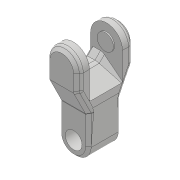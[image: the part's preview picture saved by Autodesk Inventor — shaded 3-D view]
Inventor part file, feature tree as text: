
AUTODESK INVENTOR PART (.ipt)
format: ipt  version: 2018 (Build 220112000, 112)  size: 823,296 bytes
history: native  units: mm
features: sketch x33, projected_geometry x33, extrude x31, chamfer x11, fillet x7, hole x3, mirror x1
ambient origin geometry x8: Origin, YZ Plane, XZ Plane, XY Plane, X Axis, Y Axis, Z Axis, Center Point
bodies: Solid1 (feature_tree)
feature tree (119):
  extrude  "Extrusion1"  Depth=45.0mm
  extrude  "Extrusion2"  Depth=2.25mm
  hole  "Hole1"  [1 undecoded]
  hole  "Hole2"  [1 undecoded]
  fillet  "Fillet1"  Radius=14.0mm
  extrude  "Extrusion3"  Depth=18.5mm
  extrude  "Extrusion4"  Depth=10.0mm
  extrude  "Extrusion5"  Depth=2.195mm
  extrude  "Extrusion6"  Depth=20.5mm
  hole  "Hole3"  [1 undecoded]
  extrude  "Extrusion7"  Depth=0.5mm
  extrude  "Extrusion8"  Depth=5.0mm TaperAngle=0.0deg
  extrude  "Extrusion9"  Depth=10.0mm
  extrude  "Extrusion10"  Depth=10.0mm
  extrude  "Extrusion11"  Depth=14.5mm
  extrude  "Extrusion12"  Depth=14.5mm
  extrude  "Extrusion13"  Depth=5.0mm
  extrude  "Extrusion14"  Depth=2.25mm
  extrude  "Extrusion15"  Depth=5.0mm
  extrude  "Extrusion16"  Depth=9.0mm
  extrude  "Extrusion17"  Depth=14.75mm
  chamfer  "Chamfer1"  Distance=1.0mm
  fillet  "Fillet7"  Radius=20.7mm
  fillet  "Fillet8"  Radius=32.0mm
  mirror  "Mirror1"
  extrude  "Extrusion19"  Depth=1.0mm TaperAngle=0.0deg
  extrude  "Extrusion20"  Depth=8.0mm
  extrude  "Extrusion21"  Depth=0.2mm TaperAngle=0.0deg
  extrude  "Extrusion22"  Depth=0.5mm TaperAngle=0.0deg
  extrude  "Extrusion23"  Depth=9.0mm TaperAngle=0.0deg
  extrude  "Extrusion24"  Depth=0.2mm TaperAngle=0.0deg
  chamfer  "Chamfer2"  Distance=0.2mm
  chamfer  "Chamfer8"  Distance=2.5mm Angle=45.0deg
  extrude  "Extrusion25"  Depth=0.5mm
  extrude  "Extrusion26"  Depth=2.0mm TaperAngle=0.0deg
  chamfer  "Chamfer3"  Distance=2.0mm
  chamfer  "Chamfer4"  Distance=2.0mm
  chamfer  "Chamfer5"  Distance=70.0mm
  chamfer  "Chamfer6"  Distance=15.0mm
  fillet  "Fillet9"  Radius=56.1mm
  fillet  "Fillet10"  Radius=4.0mm
  extrude  "Extrusion27"  Depth=41.6mm
  extrude  "Extrusion28"  Depth=10.0mm
  extrude  "Extrusion29"  Depth=10.0mm
  chamfer  "Chamfer7"  Distance=7.0mm
  extrude  "Extrusion30"  Depth=10.0mm
  fillet  "Fillet18"  Radius=100.0mm
  chamfer  "Chamfer9"  Distance=15.282752mm
  chamfer  "Chamfer10"  Distance=100.0mm
  chamfer  "Chamfer11"  Distance=3.0mm Angle=45.0deg
  fillet  "Fillet19"  Radius=5.0mm
  extrude  "Extrusion37"  Depth=10.0mm TaperAngle=45.0deg
  extrude  "Extrusion38"  Depth=10.0mm TaperAngle=45.0deg
  sketch  "Sketch1"  dims[d0=24.5mm d1=45.0mm]
  sketch  "Sketch2"  dims[d2=1.95mm d3=0.0mm d4=2.25mm]
  projected_geometry  "Projected Loop1"
  sketch  "Sketch3"  dims[d5=20.0mm d6=2.25mm]
  projected_geometry  "Projected Loop2"
  sketch  "Sketch4"  dims[d7=5.25mm d8=5.25mm d9=14.0mm]
  projected_geometry  "Projected Loop3"
  sketch  "Sketch5"  dims[d10=5.25mm d11=18.5mm]
  projected_geometry  "Projected Loop4"
  sketch  "Sketch6"  dims[d12=10.0mm d13=0.0mm d14=20.5mm]
  projected_geometry  "Projected Loop5"
  sketch  "Sketch7"  dims[d15=2.0mm d16=2.195mm]
  projected_geometry  "Projected Loop6"
  sketch  "Sketch8"  dims[d17=2.0mm]
  projected_geometry  "Projected Loop7"
  sketch  "Sketch9"  dims[d18=2.4mm d19=6.0mm d20=4.4mm d21=2.0mm d22=90.0deg d23=8.0mm d24=20.594885mm d25=20.5mm]
  projected_geometry  "Projected Loop8"
  projected_geometry  "Projected Loop9"
  sketch  "Sketch10"  dims[d26=26.65mm d27=2.0mm]
  projected_geometry  "Projected Loop10"
  projected_geometry  "Projected Loop11"
  sketch  "Sketch11"  dims[d28=2.0mm]
  projected_geometry  "Projected Loop12"
  sketch  "Sketch12"  dims[d29=2.4mm d30=6.0mm d31=4.4mm d32=2.0mm d33=90.0deg d34=8.0mm d35=20.594885mm d36=0.5mm]
  sketch  "Sketch13"  dims[d37=18.0mm d38=5.0mm d39=0.0mm]
  sketch  "Sketch14"  dims[d41=10.0mm d42=0.0mm d43=24.5mm]
  projected_geometry  "Projected Loop13"
  sketch  "Sketch15"  dims[d44=1.15mm d45=0.0mm d46=10.0mm]
  sketch  "Sketch16"  dims[d47=21.0mm d48=14.5mm]
  projected_geometry  "Projected Loop14"
  sketch  "Sketch17"  dims[d49=20.0mm d50=14.5mm]
  projected_geometry  "Projected Loop15"
  sketch  "Sketch18"  dims[d51=24.5mm d52=5.0mm]
  projected_geometry  "Projected Loop16"
  sketch  "Sketch19"  dims[d53=5.0mm d54=2.25mm]
  projected_geometry  "Projected Loop17"
  sketch  "Sketch20"  dims[d55=2.25mm d56=5.0mm]
  projected_geometry  "Projected Loop18"
  sketch  "Sketch25"  dims[d57=5.0mm d58=9.0mm]
  projected_geometry  "Projected Loop22"
  sketch  "Sketch26"  dims[d59=14.75mm d60=4.0mm d61=1.0mm d62=0.0mm d63=20.7mm]
  projected_geometry  "Projected Loop23"
  sketch  "Sketch27"  dims[d64=2.4mm d65=6.0mm d66=4.4mm d67=2.0mm d68=90.0deg d69=8.0mm d70=20.594885mm d72=32.0mm]
  projected_geometry  "Projected Loop24"
  sketch  "Sketch28"  dims[d73=5.0mm d74=0.0mm d75=1.0mm d76=0.0mm]
  projected_geometry  "Projected Loop25"
  sketch  "Sketch29"  dims[d77=12.25mm d78=0.0mm d80=8.0mm]
  projected_geometry  "Projected Loop26"
  sketch  "Sketch30"  dims[d81=4.5mm d82=0.0mm d84=0.2mm d85=0.0mm]
  projected_geometry  "Projected Loop27"
  sketch  "Sketch31"  dims[d86=21.0mm d87=0.5mm d88=0.0mm]
  sketch  "Sketch35"  dims[d91=8.0mm d92=0.0mm d93=9.0mm d94=0.0mm]
  projected_geometry  "Projected Loop33"
  sketch  "Sketch36"  dims[d95=5.0mm d96=0.0mm d98=0.2mm d99=0.0mm d100=0.2mm d101=0.0mm d102=2.5mm d103=2.0mm d104=45.0deg]
  projected_geometry  "Projected Loop34"
  sketch  "Sketch38"  dims[d105=1.5mm d114=0.5mm]
  projected_geometry  "Projected Loop36"
  sketch  "Sketch39"  dims[d128=2.0mm d129=0.0mm d130=2.0mm d131=0.0mm]
  projected_geometry  "Projected Loop37"
  sketch  "Sketch48"  dims[d132=40.0mm d133=2.0mm d134=0.0mm d135=2.0mm d136=0.0mm]
  projected_geometry  "Projected Loop46"
  projected_geometry  "Projected Loop47"
  sketch  "Sketch49"  dims[d137=40.0mm d138=70.0mm d139=15.0mm d140=0.0mm d141=56.1mm d142=0.0mm d143=4.0mm d144=8.0mm d145=45.0deg d146=41.6mm d147=41.0mm d148=7.0mm d149=7.0mm d150=7.0mm d151=100.0mm d152=0.0mm d153=15.282752mm d156=100.0mm d157=0.0mm d158=3.0mm d159=2.0mm d160=45.0deg d161=5.0mm d162=2.0mm d163=45.0deg d164=5.0mm d165=2.0mm d166=45.0deg d167=5.0mm d168=2.0mm d169=45.0deg d170=5.0mm d171=2.0mm d188=20.5mm d189=1.6mm d190=0.0mm d191=20.5mm d192=3.1mm d193=0.0mm d202=16.0mm d203=3.1mm d204=0.0mm d205=1.5mm d206=2.0mm d207=45.0deg d209=37.0mm d210=10.0mm d211=0.0mm d231=4.0mm d232=8.0mm d233=45.0deg d234=10.0mm d243=14.0mm d244=25.0mm d245=45.0deg d246=14.0mm d247=25.0mm d248=45.0deg d249=14.0mm d250=25.0mm d251=45.0deg d252=10.0mm d269=10.0mm d270=0.0mm d271=10.0mm d272=0.0mm]
  projected_geometry  "Projected Loop48"
  projected_geometry  "Project Cut Edges1"
  projected_geometry  "Project Cut Edges2"
note: 3 required parameter values undecoded (feature->parameter linkage not recoverable at this tier; creation-order binding heuristic only, values carry confidence <= 0.55)
